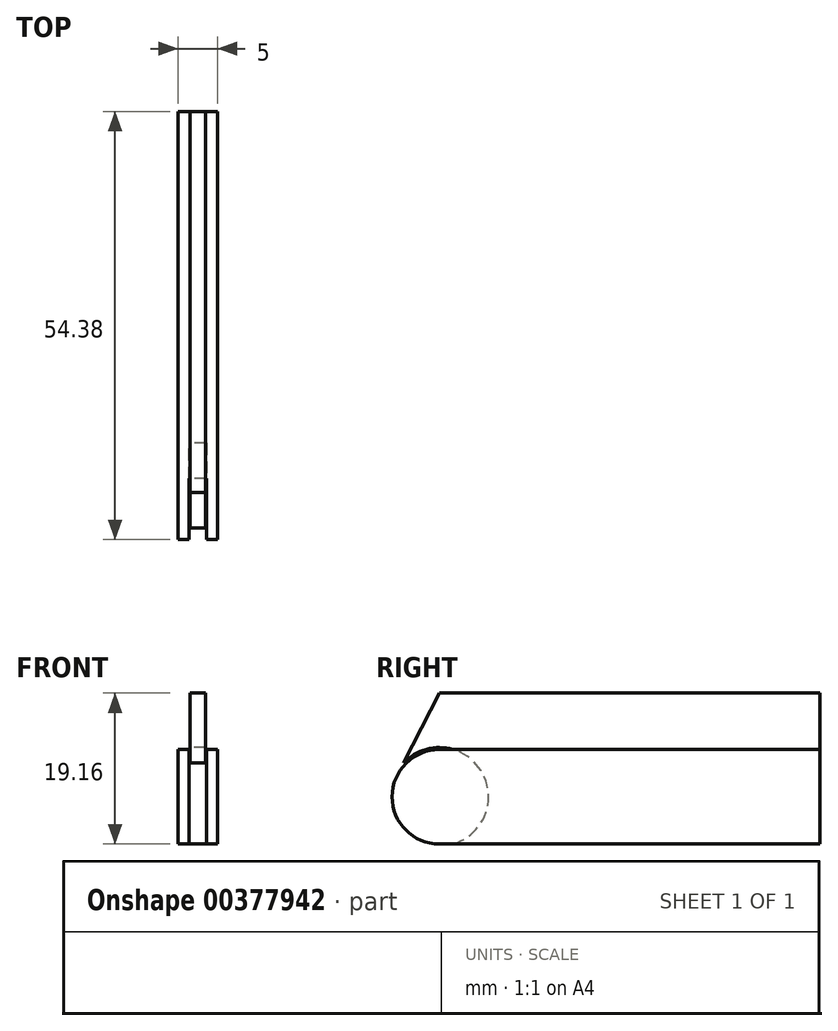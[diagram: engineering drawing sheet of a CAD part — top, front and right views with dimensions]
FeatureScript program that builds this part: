
annotation { "Feature Type Name" : "Feature", "Feature Type Description" : "" }
export const myFeature = defineFeature(function(context is Context, id is Id, definition is map)
    precondition{}
    {
        {
            var Q0;
            Q0=qCreatedBy(makeId("Right.planeOp"),FACE);
            var sketch = newSketch(context, id + "F0", { "sketchPlane" : qUnion([Q0])});
            skCircle(sketch, "E0", {"center": v(-43.22, 0) * mm, "radius": 6 * mm});
            skCircle(sketch, "E1", {"center": v(-43.22, 0) * mm, "radius": 3 * mm});
            skLineSegment(sketch, "E2", {"start": v(-43.22, 6) * mm, "end": v(5.16, 6) * mm});
            skLineSegment(sketch, "E3", {"start": v(-43.23, -6) * mm, "end": v(5.16, -6) * mm});
            skLineSegment(sketch, "E4", {"start": v(5.16, -6) * mm, "end": v(5.16, 6) * mm});
            skSolve(sketch);
        }
        {
            var Q0;
            Q0=qCreatedBy(makeId("Right.planeOp"),FACE);
            var sketch = newSketch(context, id + "F1", { "sketchPlane" : qUnion([Q0])});
            skCircle(sketch, "E5", {"center": v(-43.22, 0) * mm, "radius": 3 * mm});
            skArc(sketch, "E6", {"start": v(-48.56, 2.73) * mm, "mid": v(-43.7, -5.98) * mm, "end": v(-37.5, 1.83) * mm});
            skLineSegment(sketch, "E7", {"start": v(-35.44, 6) * mm, "end": v(5.16, 6) * mm});
            skLineSegment(sketch, "E8", {"start": v(5.16, 6) * mm, "end": v(5.16, 13.16) * mm});
            skLineSegment(sketch, "E9", {"start": v(5.16, 13.16) * mm, "end": v(-43.22, 13.16) * mm});
            skLineSegment(sketch, "E10", {"start": v(-43.22, 13.16) * mm, "end": v(-48.56, 2.73) * mm});
            skLineSegment(sketch, "E11", {"start": v(-37.5, 1.83) * mm, "end": v(-35.44, 6) * mm});
            skPoint(sketch, "E12.orphan", {"position": v(-43.22, 6) * mm});
            skSolve(sketch);
        }
        {
            var Q0;
            {var subQ0=sQuery(id+"F0.wireOp",EDGE,"E2");Q0=makeQuery(id+"F0.imprint","IMPRINT",FACE,{"disambiguationData":[TD([[makeQuery(id+"F0.imprint","IMPRINT",EDGE,{"derivedFrom":subQ0}),-1.0]])]});}
            var Q1;
            Q1=makeQuery(id+"F0.imprint","IMPRINT",FACE,{"disambiguationData":[TD([[makeQuery(id+"F0.imprint","IMPRINT",EDGE,{"derivedFrom":sQuery(id+"F0.wireOp",EDGE,"E1")}),-1.0]])]});
            extrude(context, id + "F2", {"entities" : qUnion([Q0, Q1]), "endBound" : BoundingType.SYMMETRIC, "depth" : 5 * mm});
        }
        {
            var Q0;
            Q0=makeQuery(id+"F1.imprint","IMPRINT",FACE,{"disambiguationData":[TD([[makeQuery(id+"F1.imprint","IMPRINT",EDGE,{"derivedFrom":sQuery(id+"F1.wireOp",EDGE,"E5")}),-1.0]])]});
            extrude(context, id + "F3", {"entities" : qUnion([Q0]), "endBound" : BoundingType.SYMMETRIC, "depth" : 2 * mm});
        }
        {
            var Q0;
            Q0=makeQuery(id+"F0.imprint","IMPRINT",FACE,{"disambiguationData":[TD([[makeQuery(id+"F0.imprint","IMPRINT",EDGE,{"derivedFrom":sQuery(id+"F0.wireOp",EDGE,"E1")}),1.0]])]});
            extrude(context, id + "F4", {"entities" : qUnion([Q0]), "operationType" : NewBodyOperationType.ADD, "endBound" : BoundingType.SYMMETRIC, "depth" : 5 * mm});
        }
        {
            var Q0;
            Q0=qCreatedBy(makeId("Right.planeOp"),FACE);
            var sketch = newSketch(context, id + "F5", { "sketchPlane" : qUnion([Q0])});
            skCircle(sketch, "E13", {"center": v(-43.22, 0) * mm, "radius": 6.25 * mm});
            skSolve(sketch);
        }
        {
            var Q0;
            Q0 = qSketchRegion(id + "F5", true);
            extrude(context, id + "F6", {"entities" : qUnion([Q0]), "operationType" : NewBodyOperationType.REMOVE, "endBound" : BoundingType.SYMMETRIC, "depth" : 2.2 * mm});
        }
    });
